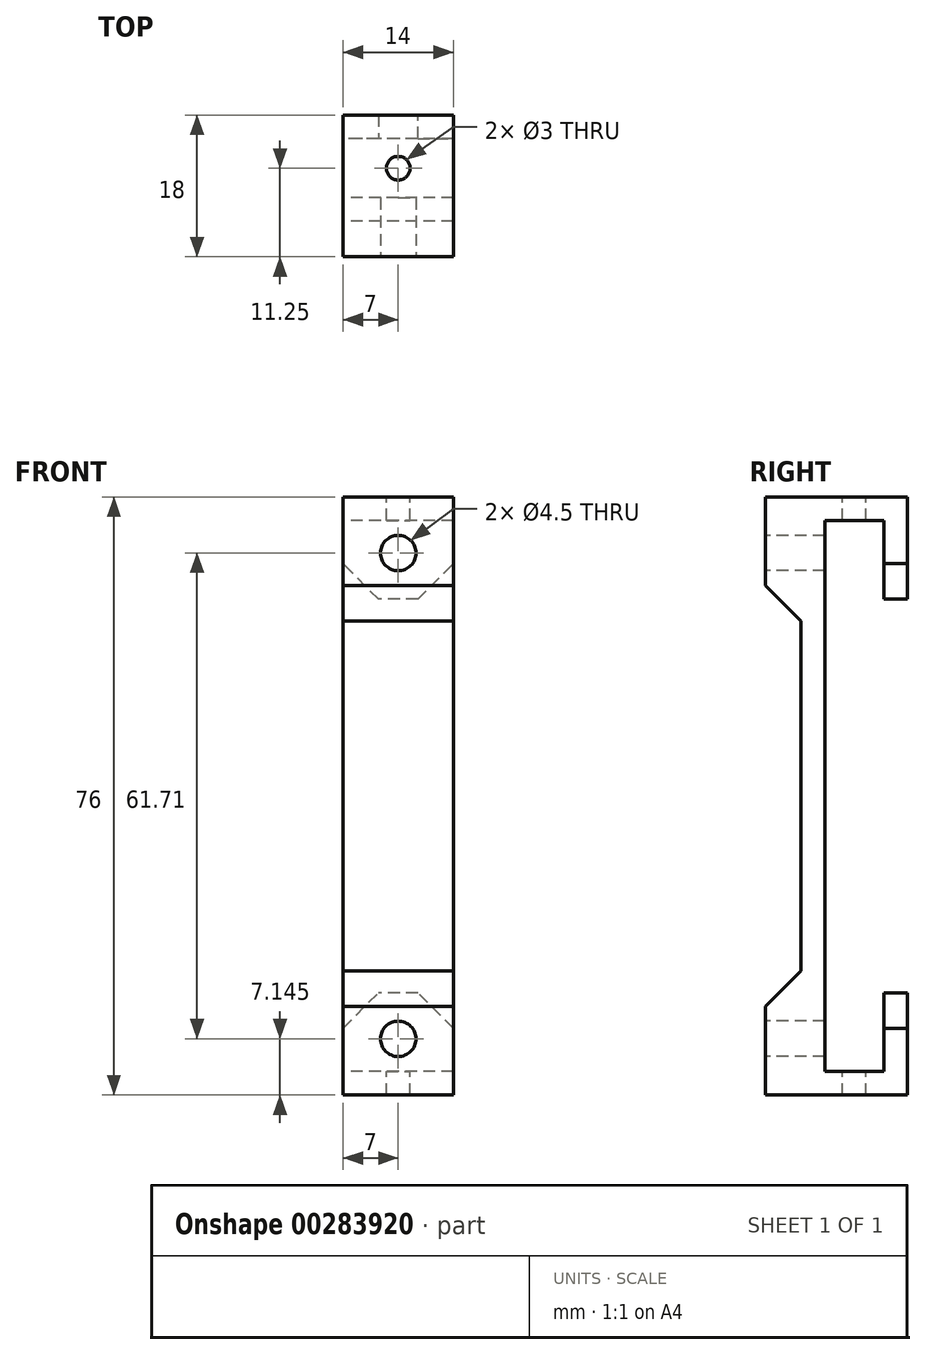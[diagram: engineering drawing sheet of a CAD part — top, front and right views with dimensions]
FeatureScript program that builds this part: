
annotation { "Feature Type Name" : "Feature", "Feature Type Description" : "" }
export const myFeature = defineFeature(function(context is Context, id is Id, definition is map)
    precondition{}
    {
        {
            var Q0;
            Q0=qCreatedBy(makeId("Right.planeOp"),FACE);
            var sketch = newSketch(context, id + "F0", { "sketchPlane" : qUnion([Q0])});
            skLineSegment(sketch, "E0.bottom", {"start": v(3.75, 35) * mm, "end": v(-3.75, 35) * mm});
            skLineSegment(sketch, "E0.top", {"start": v(3.75, -35) * mm, "end": v(-3.75, -35) * mm});
            skLineSegment(sketch, "E0.left", {"start": v(3.75, 35) * mm, "end": v(3.75, -35) * mm, "construction": true});
            skLineSegment(sketch, "E0.right", {"start": v(-3.75, 35) * mm, "end": v(-3.75, -35) * mm});
            skPoint(sketch, "E0.middle", {"position": v(0, 0) * mm});
            skLineSegment(sketch, "E1", {"start": v(3.75, 35) * mm, "end": v(3.75, 25) * mm});
            skLineSegment(sketch, "E2", {"start": v(3.75, 25) * mm, "end": v(6.75, 25) * mm});
            skLineSegment(sketch, "E3", {"start": v(6.75, 25) * mm, "end": v(6.75, 38) * mm});
            skLineSegment(sketch, "E4", {"start": v(6.75, 38) * mm, "end": v(-11.25, 38) * mm});
            skLineSegment(sketch, "E5", {"start": v(-11.25, 38) * mm, "end": v(-11.25, 26.7) * mm});
            skLineSegment(sketch, "E6", {"start": v(-11.25, 26.7) * mm, "end": v(-6.75, 26.7) * mm});
            skLineSegment(sketch, "E7", {"start": v(0, 0) * mm, "end": v(42, 0) * mm, "construction": true});
            skLineSegment(sketch, "E8.MirrorCS", {"start": v(-11.25, -26.7) * mm, "end": v(-6.75, -26.7) * mm});
            skLineSegment(sketch, "E9.MirrorCS", {"start": v(-11.25, -38) * mm, "end": v(-11.25, -26.7) * mm});
            skLineSegment(sketch, "E10.MirrorCS", {"start": v(6.75, -38) * mm, "end": v(-11.25, -38) * mm});
            skLineSegment(sketch, "E11.MirrorCS", {"start": v(6.75, -25) * mm, "end": v(6.75, -38) * mm});
            skLineSegment(sketch, "E12.MirrorCS", {"start": v(3.75, -25) * mm, "end": v(6.75, -25) * mm});
            skLineSegment(sketch, "E13.MirrorCS", {"start": v(3.75, -35) * mm, "end": v(3.75, -25) * mm});
            skLineSegment(sketch, "E14", {"start": v(-6.75, 26.7) * mm, "end": v(-6.75, -26.7) * mm});
            skLineSegment(sketch, "E15", {"start": v(-6.75, 26.7) * mm, "end": v(-6.75, 35) * mm, "construction": true});
            skLineSegment(sketch, "E16", {"start": v(-6.75, 35) * mm, "end": v(-3.75, 35) * mm, "construction": true});
            skPoint(sketch, "E17", {"position": v(-6.75, 30.86) * mm});
            skSolve(sketch);
        }
        {
            var Q0;
            Q0 = qSketchRegion(id + "F0", true);
            extrude(context, id + "F1", {"entities" : qUnion([Q0]), "endBound" : BoundingType.SYMMETRIC, "depth" : 14 * mm});
        }
        {
            var Q0;
            Q0=makeQuery(id+"F1.opExtrude","SWEPT_EDGE",EDGE,{"disambiguationData":[OSD([sQuery(id+"F0.wireOp",EDGE,"E6"),sQuery(id+"F0.wireOp",EDGE,"E14")])]});
            var Q1;
            Q1=makeQuery(id+"F1.opExtrude","SWEPT_EDGE",EDGE,{"disambiguationData":[OSD([sQuery(id+"F0.wireOp",EDGE,"E8.MirrorCS"),sQuery(id+"F0.wireOp",EDGE,"E14")])]});
            var Q2;
            Q2=makeQuery(id+"F1.opExtrude","CAP_EDGE",EDGE,{"disambiguationData":[OSD([sQuery(id+"F0.wireOp",EDGE,"E2")])],"isStart":true});
            var Q3;
            Q3=makeQuery(id+"F1.opExtrude","CAP_EDGE",EDGE,{"disambiguationData":[OSD([sQuery(id+"F0.wireOp",EDGE,"E2")])],"isStart":false});
            var Q4;
            Q4=makeQuery(id+"F1.opExtrude","CAP_EDGE",EDGE,{"disambiguationData":[OSD([sQuery(id+"F0.wireOp",EDGE,"E12.MirrorCS")])],"isStart":true});
            var Q5;
            Q5=makeQuery(id+"F1.opExtrude","CAP_EDGE",EDGE,{"disambiguationData":[OSD([sQuery(id+"F0.wireOp",EDGE,"E12.MirrorCS")])],"isStart":false});
            chamfer(context, id + "F2", {"entities" : qUnion([Q0, Q1, Q2, Q3, Q4, Q5]), "width" : 4.5 * mm, "tangentPropagation" : true});
        }
        {
            var Q0;
            Q0=makeQuery(id+"F1.opExtrude","SWEPT_FACE",FACE,{"disambiguationData":[OSD([sQuery(id+"F0.wireOp",EDGE,"E5")])]});
            var sketch = newSketch(context, id + "F3", { "sketchPlane" : qUnion([Q0])});
            skCircle(sketch, "E18", {"center": v(0, 30.85) * mm, "radius": 2.25 * mm});
            skLineSegment(sketch, "E19", {"start": v(0, 0) * mm, "end": v(29.18, 0) * mm, "construction": true});
            skCircle(sketch, "E20.MirrorC", {"center": v(0, -30.85) * mm, "radius": 2.25 * mm});
            skLineSegment(sketch, "E21.0", {"start": v(7, 35) * mm, "end": v(7, -35) * mm, "construction": true});
            skLineSegment(sketch, "E22", {"start": v(7, 35) * mm, "end": v(-7, 35) * mm, "construction": true});
            skLineSegment(sketch, "E23", {"start": v(0, 26.7) * mm, "end": v(0, 35) * mm, "construction": true});
            skSolve(sketch);
        }
        {
            var Q0;
            Q0 = qSketchRegion(id + "F3", true);
            extrude(context, id + "F4", {"entities" : qUnion([Q0]), "operationType" : NewBodyOperationType.REMOVE, "endBound" : BoundingType.UP_TO_NEXT, "oppositeDirection" : true, "depth" : 25 * mm});
        }
        {
            var Q0;
            Q0=makeQuery(id+"F1.opExtrude","SWEPT_FACE",FACE,{"disambiguationData":[OSD([sQuery(id+"F0.wireOp",EDGE,"E4")])]});
            var sketch = newSketch(context, id + "F5", { "sketchPlane" : qUnion([Q0])});
            skLineSegment(sketch, "E24.0", {"start": v(-7, 3.75) * mm, "end": v(-7, -3.75) * mm, "construction": true});
            skLineSegment(sketch, "E25", {"start": v(-7, 0) * mm, "end": v(7, 0) * mm, "construction": true});
            skCircle(sketch, "E26", {"center": v(0, 0) * mm, "radius": 1.5 * mm});
            skPoint(sketch, "E26.perimeterSnap0", {"position": v(0, 0) * mm});
            skPoint(sketch, "E26.perimeterSnap1", {"position": v(7, -2.25) * mm});
            skSolve(sketch);
        }
        {
            var Q0;
            Q0 = qSketchRegion(id + "F5", true);
            extrude(context, id + "F6", {"entities" : qUnion([Q0]), "operationType" : NewBodyOperationType.REMOVE, "endBound" : BoundingType.THROUGH_ALL, "oppositeDirection" : true, "depth" : 25 * mm});
        }
    });
